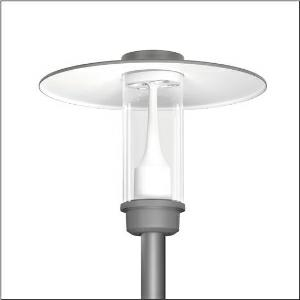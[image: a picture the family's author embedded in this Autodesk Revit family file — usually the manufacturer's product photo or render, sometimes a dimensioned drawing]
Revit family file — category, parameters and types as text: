
# Revit family: litepole_2_iq___st1_2a_5xa5425ef14h000022_7f5b
name_source: partatom
category: Lighting Fixtures
units: mm (PartAtom-declared; Revit-internal decimal feet)

## family parameters
Cut with Voids When Loaded = No
Host = Face
Light Source = No
Part Type = Normal
Room Calculation Point = No
Round Connector Dimension = Use Diameter
Shared = No

## types (1)
- --- (1 x LED, 1550 lm, 10.5 W, 3000K)
    Apparent Load = 11 VA
    CIE Flux Codes = 22 60 92 98 100
    Color Rendering = 70
    Color Temperature = 3000K
    Default Elevation = 1800 mm
    Description = Litepole 2 iQ, mast luminaire, Module 540 iQ-SR, primary light control with 3 zone facetted reflector, of plastic, silver coated, highly specular, structured, primary optical cover: cover, of PMMA, transparent, light distribution: ST1.2a, light emission: direct distribution, primary light characteristic: asymmetric, installation type: post-top, LED, High Power LED, rated luminous flux: 1.550lm, luminous efficacy: 148lm/W, light colour: 730, colour temperature: 3000K, control gear: iQ Street-Remote, control: Street-Remote, Auto-Match, Temp-Guard, Lumen-Switch, Night-Set, Smart-Wire, Light-Fading, Desk-Remote (wireless, voltage-free reading and setting of iQ features in the workshop via application-optimized NFC function/RFID function), optimised constant luminous flux control (CLO 2.0), pre-setting: logarithmic dimming characteristic, mains connection: 230..240V, AC, 50/60Hz, connection cable pre-assembled, cable length: 5,5m, wiring characteristics: H07RN-F, start of lifetime: 11W, end of service life: 11W, reduction: 5W, luminaire housing, upper part, of aluminium, coated, SITECO metallic grey (DB 702S), diameter: 750mm, height: 590mm, spigot size: d x l = 76 x 70mm (post-top) | with reducer (optional accessory) 60 x 70mm, mounting height: 3..5m, post-top mast mounting element, of diecast aluminium, coated, SITECO metallic grey (DB 702S), Module 540 iQ-SR, traffic white (RAL 9016), equipment: standard, protection rating (complete): IP65, insulation class (complete): insulation class II (safety insulation), certification: CE, ENEC, VDE, packaging unit: 1 piece

Light Distribution: ST1.2a
    Height = 590 mm
    Lamp = 1 x LED
    Lamp Light Flux = 1550 lm
    Lamp Power = 10.5 W
    Lamp count = 1
    Length = 750 mm
    Luminous efficacy = 148 lm/W
    Manufacturer = Siteco
    ModVariant = No
    Model = 5XA5425EF14H000022
    Number of Poles = 1
    OnlyDefault = Yes
    Power Factor = 1
    Product Name = Litepole 2 iQ | ST1.2a
    Product group = mast luminaire | pylon top
    ProductGroupID = 6100
    Protection Class = Protection class II
    Protection Degree = IP 65
    RLX_Detail_Level = 1
    RLX_Emergency_Light_Flux = 0 lm
    RLX_Emergency_Type = 0
    RLX_Emergency_Type_DB = No
    RlxData = <blob elided: 30961 chars, md5=fb896e71>
    Socket = socket
    Standby Power = 0 W
    System Light Flux = 1550 lm
    System Power = 11 W
    Type Comments = factory setting: luminous flux: 100 % | dim-lin: 254 | 419 mA
    Type Image = l_1006518.jpg
    URL = http://relux.com
    VarID = @adj_190043
    Voltage = 0 V
    Weight = 0.00 kg
    Width = 0 mm  [stored 0 ft]

note: [stored X ft] marks values corroborated as IEEE doubles in the binary element streams (Revit-internal decimal feet)

## geometry (parser evidence)
native form markers: Blend x4, Sweep x7
no freeform markers — native parametric forms only
